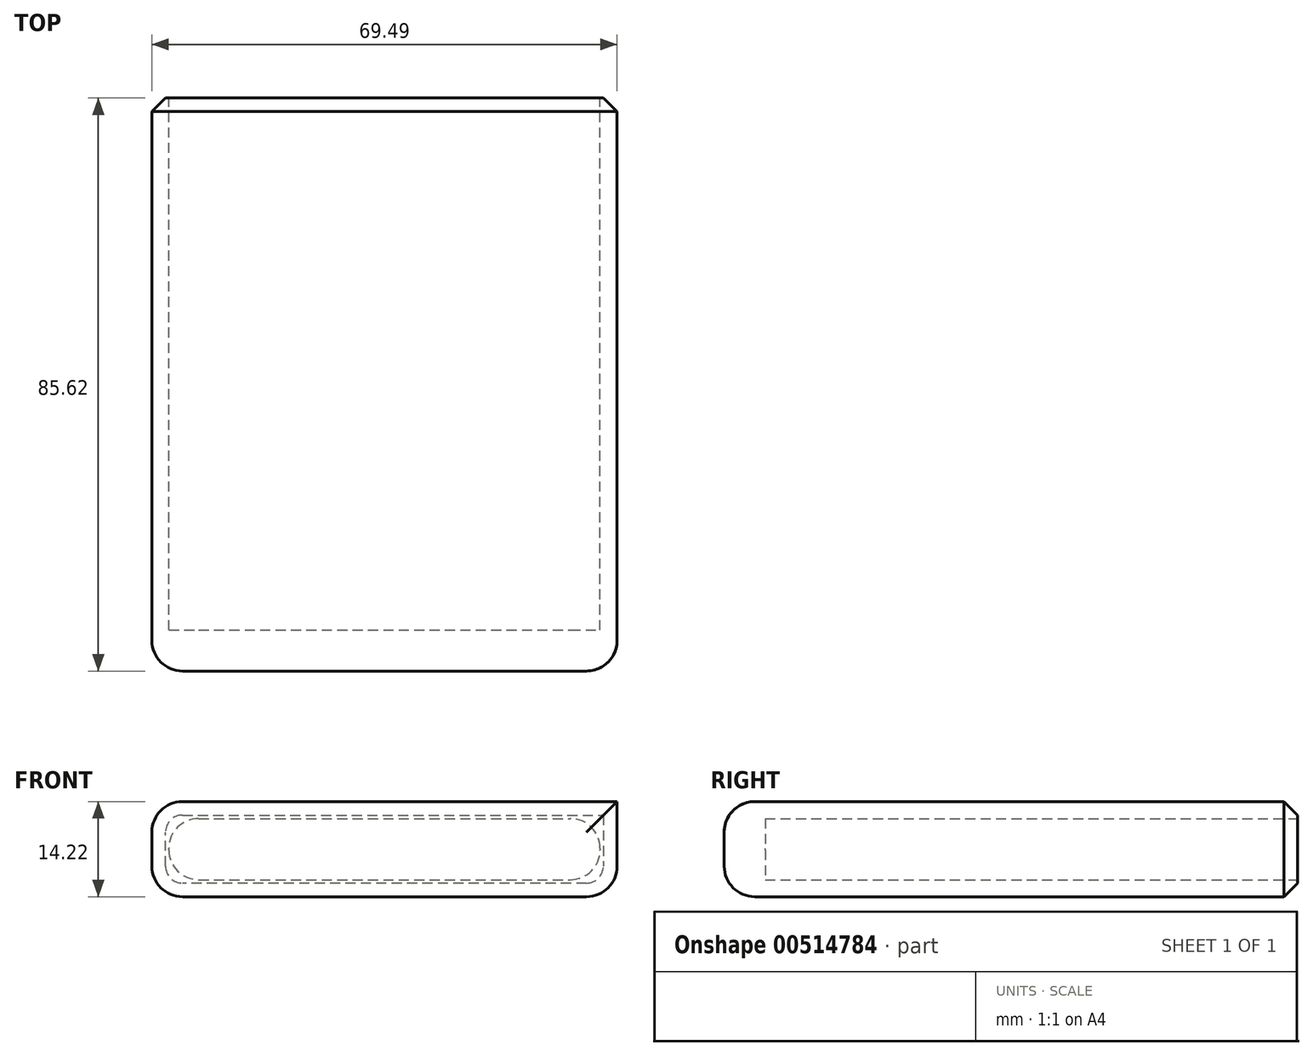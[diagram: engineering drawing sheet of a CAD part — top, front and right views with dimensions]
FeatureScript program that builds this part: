
annotation { "Feature Type Name" : "Feature", "Feature Type Description" : "" }
export const myFeature = defineFeature(function(context is Context, id is Id, definition is map)
    precondition{}
    {
        {
            var Q0;
            Q0=qCreatedBy(makeId("Front.planeOp"),FACE);
            var sketch = newSketch(context, id + "F0", { "sketchPlane" : qUnion([Q0])});
            skLineSegment(sketch, "E0.bottom", {"start": v(0, 0) * mm, "end": v(64.41, 0) * mm});
            skLineSegment(sketch, "E0.top", {"start": v(0, 9.14) * mm, "end": v(64.41, 9.14) * mm});
            skLineSegment(sketch, "E0.left", {"start": v(0, 0) * mm, "end": v(0, 9.14) * mm});
            skLineSegment(sketch, "E0.right", {"start": v(64.41, 0) * mm, "end": v(64.41, 9.14) * mm});
            skLineSegment(sketch, "E1.0", {"start": v(0, 11.68) * mm, "end": v(64.41, 11.68) * mm});
            skLineSegment(sketch, "E2.0", {"start": v(-2.54, 0) * mm, "end": v(-2.54, 9.14) * mm});
            skLineSegment(sketch, "E3.0", {"start": v(0, -2.54) * mm, "end": v(64.41, -2.54) * mm});
            skLineSegment(sketch, "E4.0", {"start": v(66.95, 0) * mm, "end": v(66.95, 9.14) * mm});
            skLineSegment(sketch, "E5.bottom", {"start": v(64.41, 9.14) * mm, "end": v(66.95, 9.14) * mm});
            skLineSegment(sketch, "E5.top", {"start": v(64.41, 11.68) * mm, "end": v(66.95, 11.68) * mm});
            skLineSegment(sketch, "E5.left", {"start": v(64.41, 9.14) * mm, "end": v(64.41, 11.68) * mm});
            skLineSegment(sketch, "E5.right", {"start": v(66.95, 9.14) * mm, "end": v(66.95, 11.68) * mm});
            skLineSegment(sketch, "E6.bottom", {"start": v(66.95, 11.68) * mm, "end": v(-2.54, 11.68) * mm});
            skLineSegment(sketch, "E6.top", {"start": v(66.95, -2.54) * mm, "end": v(-2.54, -2.54) * mm});
            skLineSegment(sketch, "E6.left", {"start": v(66.95, 11.68) * mm, "end": v(66.95, -2.54) * mm});
            skLineSegment(sketch, "E6.right", {"start": v(-2.54, 11.68) * mm, "end": v(-2.54, -2.54) * mm});
            skSolve(sketch);
        }
        {
            var Q0;
            Q0=makeQuery(id+"F0.imprint","IMPRINT",FACE,{"disambiguationData":[TD([[makeQuery(id+"F0.imprint","IMPRINT",EDGE,{"derivedFrom":sQuery(id+"F0.wireOp",EDGE,"E0.bottom")}),-1.0]])]});
            var Q1;
            {var subQ0=sQuery(id+"F0.wireOp",EDGE,"E5.bottom");Q1=makeQuery(id+"F0.imprint","IMPRINT",FACE,{"disambiguationData":[TD([[makeQuery(id+"F0.imprint","IMPRINT",EDGE,{"derivedFrom":subQ0}),1.0]])]});}
            extrude(context, id + "F1", {"entities" : qUnion([Q0, Q1]), "depth" : 85.62 * mm, "offsetDistance" : 25.4 * mm});
        }
        {
            var Q0;
            Q0=makeQuery(id+"F1.opExtrude","SWEPT_FACE",FACE,{"disambiguationData":[OSD([sQuery(id+"F0.wireOp",EDGE,"E0.right")])]});
            var sketch = newSketch(context, id + "F2", { "sketchPlane" : qUnion([Q0])});
            skLineSegment(sketch, "E7.bottom", {"start": v(85.62, 9.14) * mm, "end": v(84.58, 9.14) * mm});
            skLineSegment(sketch, "E7.top", {"start": v(85.62, 0) * mm, "end": v(84.58, 0) * mm});
            skLineSegment(sketch, "E7.left", {"start": v(85.62, 9.14) * mm, "end": v(85.62, 0) * mm});
            skLineSegment(sketch, "E7.right", {"start": v(84.58, 9.14) * mm, "end": v(84.58, 0) * mm});
            skSolve(sketch);
        }
        {
            var Q0;
            Q0=makeQuery(id+"F2.imprint","IMPRINT",FACE,{"disambiguationData":[TD([[makeQuery(id+"F2.imprint","IMPRINT",EDGE,{"derivedFrom":sQuery(id+"F2.wireOp",EDGE,"E7.bottom")}),1.0]])]});
            extrude(context, id + "F3", {"entities" : qUnion([Q0]), "operationType" : NewBodyOperationType.ADD, "depth" : 66.04 * mm, "offsetDistance" : 25.4 * mm});
        }
        {
            var Q0;
            Q0=makeQuery(id+"F1.opExtrude","CAP_EDGE",EDGE,{"disambiguationData":[OSD([sQuery(id+"F0.wireOp",EDGE,"E6.bottom")])],"isStart":false});
            var Q1;
            Q1=makeQuery(id+"F1.opExtrude","CAP_EDGE",EDGE,{"disambiguationData":[OSD([sQuery(id+"F0.wireOp",EDGE,"E6.right")])],"isStart":false});
            var Q2;
            Q2=makeQuery(id+"F1.opExtrude","CAP_EDGE",EDGE,{"disambiguationData":[OSD([sQuery(id+"F0.wireOp",EDGE,"E6.top")])],"isStart":false});
            var Q3;
            Q3=makeQuery(id+"F1.opExtrude","CAP_EDGE",EDGE,{"disambiguationData":[OSD([sQuery(id+"F0.wireOp",EDGE,"E6.left")])],"isStart":false});
            var Q4;
            Q4=makeQuery(id+"F1.opExtrude","SWEPT_EDGE",EDGE,{"disambiguationData":[OSD([sQuery(id+"F0.wireOp",EDGE,"E6.top"),sQuery(id+"F0.wireOp",EDGE,"E6.right")])]});
            var Q5;
            Q5=makeQuery(id+"F1.opExtrude","SWEPT_EDGE",EDGE,{"disambiguationData":[OSD([sQuery(id+"F0.wireOp",EDGE,"E6.bottom"),sQuery(id+"F0.wireOp",EDGE,"E6.right")])]});
            var Q6;
            Q6=makeQuery(id+"F1.opExtrude","SWEPT_EDGE",EDGE,{"disambiguationData":[OSD([sQuery(id+"F0.wireOp",EDGE,"E6.top"),sQuery(id+"F0.wireOp",EDGE,"E6.left")])]});
            var Q7;
            Q7=makeQuery(id+"F1.opExtrude","SWEPT_EDGE",EDGE,{"disambiguationData":[OSD([sQuery(id+"F0.wireOp",EDGE,"E6.bottom"),sQuery(id+"F0.wireOp",EDGE,"E6.left")])]});
            fillet(context, id + "F4", {"entities" : qUnion([Q0, Q1, Q2, Q3, Q4, Q5, Q6, Q7]), "radius" : 4.57 * mm, "tangentPropagation" : true, "allowEdgeOverflow" : false});
        }
        {
            var Q0;
            Q0=makeQuery(id+"F1.opExtrude","CAP_EDGE",EDGE,{"disambiguationData":[OSD([sQuery(id+"F0.wireOp",EDGE,"E6.top")])],"isStart":true});
            var Q1;
            {var subQ0=sQuery(id+"F0.wireOp",EDGE,"E6.left");var subQ1=sQuery(id+"F0.wireOp",EDGE,"E6.top");Q1=makeQuery(id+"F4.opFillet","BLEND_EDGE",EDGE,{"blendedFrom":[makeQuery(id+"F1.opExtrude","SWEPT_EDGE",EDGE,{"disambiguationData":[OSD([subQ1,subQ0])]}),makeQuery(id+"F1.opExtrude","CAP_FACE",FACE,{"disambiguationData":[OSD([sQuery(id+"F0.wireOp",EDGE,"E0.bottom"),sQuery(id+"F0.wireOp",EDGE,"E0.top"),sQuery(id+"F0.wireOp",EDGE,"E0.left"),sQuery(id+"F0.wireOp",EDGE,"E0.right"),sQuery(id+"F0.wireOp",EDGE,"E6.bottom"),subQ1,subQ0,sQuery(id+"F0.wireOp",EDGE,"E6.right")])],"isStart":true})],"blendedInto":[makeQuery(id+"F1.opExtrude","CAP_FACE",FACE,{"disambiguationData":[OSD([sQuery(id+"F0.wireOp",EDGE,"E0.bottom"),sQuery(id+"F0.wireOp",EDGE,"E0.top"),sQuery(id+"F0.wireOp",EDGE,"E0.left"),sQuery(id+"F0.wireOp",EDGE,"E0.right"),sQuery(id+"F0.wireOp",EDGE,"E6.bottom"),subQ1,subQ0,sQuery(id+"F0.wireOp",EDGE,"E6.right")])],"isStart":true})]});}
            var Q2;
            Q2=makeQuery(id+"F1.opExtrude","CAP_EDGE",EDGE,{"disambiguationData":[OSD([sQuery(id+"F0.wireOp",EDGE,"E6.left")])],"isStart":true});
            var Q3;
            {var subQ0=sQuery(id+"F0.wireOp",EDGE,"E6.left");var subQ1=sQuery(id+"F0.wireOp",EDGE,"E6.bottom");Q3=makeQuery(id+"F4.opFillet","BLEND_EDGE",EDGE,{"blendedFrom":[makeQuery(id+"F1.opExtrude","SWEPT_EDGE",EDGE,{"disambiguationData":[OSD([subQ1,subQ0])]}),makeQuery(id+"F1.opExtrude","CAP_FACE",FACE,{"disambiguationData":[OSD([sQuery(id+"F0.wireOp",EDGE,"E0.bottom"),sQuery(id+"F0.wireOp",EDGE,"E0.top"),sQuery(id+"F0.wireOp",EDGE,"E0.left"),sQuery(id+"F0.wireOp",EDGE,"E0.right"),subQ1,sQuery(id+"F0.wireOp",EDGE,"E6.top"),subQ0,sQuery(id+"F0.wireOp",EDGE,"E6.right")])],"isStart":true})],"blendedInto":[makeQuery(id+"F1.opExtrude","CAP_FACE",FACE,{"disambiguationData":[OSD([sQuery(id+"F0.wireOp",EDGE,"E0.bottom"),sQuery(id+"F0.wireOp",EDGE,"E0.top"),sQuery(id+"F0.wireOp",EDGE,"E0.left"),sQuery(id+"F0.wireOp",EDGE,"E0.right"),subQ1,sQuery(id+"F0.wireOp",EDGE,"E6.top"),subQ0,sQuery(id+"F0.wireOp",EDGE,"E6.right")])],"isStart":true})]});}
            var Q4;
            Q4=makeQuery(id+"F1.opExtrude","CAP_EDGE",EDGE,{"disambiguationData":[OSD([sQuery(id+"F0.wireOp",EDGE,"E6.bottom")])],"isStart":true});
            var Q5;
            {var subQ0=sQuery(id+"F0.wireOp",EDGE,"E6.right");var subQ1=sQuery(id+"F0.wireOp",EDGE,"E6.bottom");Q5=makeQuery(id+"F4.opFillet","BLEND_EDGE",EDGE,{"blendedFrom":[makeQuery(id+"F1.opExtrude","SWEPT_EDGE",EDGE,{"disambiguationData":[OSD([subQ1,subQ0])]}),makeQuery(id+"F1.opExtrude","CAP_FACE",FACE,{"disambiguationData":[OSD([sQuery(id+"F0.wireOp",EDGE,"E0.bottom"),sQuery(id+"F0.wireOp",EDGE,"E0.top"),sQuery(id+"F0.wireOp",EDGE,"E0.left"),sQuery(id+"F0.wireOp",EDGE,"E0.right"),subQ1,sQuery(id+"F0.wireOp",EDGE,"E6.top"),sQuery(id+"F0.wireOp",EDGE,"E6.left"),subQ0])],"isStart":true})],"blendedInto":[makeQuery(id+"F1.opExtrude","CAP_FACE",FACE,{"disambiguationData":[OSD([sQuery(id+"F0.wireOp",EDGE,"E0.bottom"),sQuery(id+"F0.wireOp",EDGE,"E0.top"),sQuery(id+"F0.wireOp",EDGE,"E0.left"),sQuery(id+"F0.wireOp",EDGE,"E0.right"),subQ1,sQuery(id+"F0.wireOp",EDGE,"E6.top"),sQuery(id+"F0.wireOp",EDGE,"E6.left"),subQ0])],"isStart":true})]});}
            var Q6;
            Q6=makeQuery(id+"F1.opExtrude","CAP_EDGE",EDGE,{"disambiguationData":[OSD([sQuery(id+"F0.wireOp",EDGE,"E6.right")])],"isStart":true});
            var Q7;
            {var subQ0=sQuery(id+"F0.wireOp",EDGE,"E6.right");var subQ1=sQuery(id+"F0.wireOp",EDGE,"E6.top");Q7=makeQuery(id+"F4.opFillet","BLEND_EDGE",EDGE,{"blendedFrom":[makeQuery(id+"F1.opExtrude","SWEPT_EDGE",EDGE,{"disambiguationData":[OSD([subQ1,subQ0])]}),makeQuery(id+"F1.opExtrude","CAP_FACE",FACE,{"disambiguationData":[OSD([sQuery(id+"F0.wireOp",EDGE,"E0.bottom"),sQuery(id+"F0.wireOp",EDGE,"E0.top"),sQuery(id+"F0.wireOp",EDGE,"E0.left"),sQuery(id+"F0.wireOp",EDGE,"E0.right"),sQuery(id+"F0.wireOp",EDGE,"E6.bottom"),subQ1,sQuery(id+"F0.wireOp",EDGE,"E6.left"),subQ0])],"isStart":true})],"blendedInto":[makeQuery(id+"F1.opExtrude","CAP_FACE",FACE,{"disambiguationData":[OSD([sQuery(id+"F0.wireOp",EDGE,"E0.bottom"),sQuery(id+"F0.wireOp",EDGE,"E0.top"),sQuery(id+"F0.wireOp",EDGE,"E0.left"),sQuery(id+"F0.wireOp",EDGE,"E0.right"),sQuery(id+"F0.wireOp",EDGE,"E6.bottom"),subQ1,sQuery(id+"F0.wireOp",EDGE,"E6.left"),subQ0])],"isStart":true})]});}
            chamfer(context, id + "F5", {"entities" : qUnion([Q0, Q1, Q2, Q3, Q4, Q5, Q6, Q7]), "width" : 2.03 * mm, "tangentPropagation" : true});
        }
        {
            var Q0;
            Q0=makeQuery(id+"F1.opExtrude","SWEPT_EDGE",EDGE,{"disambiguationData":[OSD([sQuery(id+"F0.wireOp",EDGE,"E0.top"),sQuery(id+"F0.wireOp",EDGE,"E0.right"),sQuery(id+"F0.wireOp",EDGE,"E5.bottom"),sQuery(id+"F0.wireOp",EDGE,"E5.left")])]});
            var Q1;
            Q1=makeQuery(id+"F1.opExtrude","SWEPT_EDGE",EDGE,{"disambiguationData":[OSD([sQuery(id+"F0.wireOp",EDGE,"E0.bottom"),sQuery(id+"F0.wireOp",EDGE,"E0.right")])]});
            var Q2;
            Q2=makeQuery(id+"F1.opExtrude","SWEPT_EDGE",EDGE,{"disambiguationData":[OSD([sQuery(id+"F0.wireOp",EDGE,"E0.top"),sQuery(id+"F0.wireOp",EDGE,"E0.left")])]});
            var Q3;
            Q3=makeQuery(id+"F1.opExtrude","SWEPT_EDGE",EDGE,{"disambiguationData":[OSD([sQuery(id+"F0.wireOp",EDGE,"E0.bottom"),sQuery(id+"F0.wireOp",EDGE,"E0.left")])]});
            fillet(context, id + "F6", {"entities" : qUnion([Q0, Q1, Q2, Q3]), "radius" : 4.44 * mm, "tangentPropagation" : true, "allowEdgeOverflow" : false});
        }
        {
            var Q0;
            Q0=makeQuery(id+"F3.opExtrude","SWEPT_FACE",FACE,{"disambiguationData":[OSD([sQuery(id+"F2.wireOp",EDGE,"E7.right")])]});
            extrude(context, id + "F7", {"entities" : qUnion([Q0]), "operationType" : NewBodyOperationType.ADD, "depth" : 5.08 * mm, "offsetDistance" : 25.4 * mm});
        }
    });
